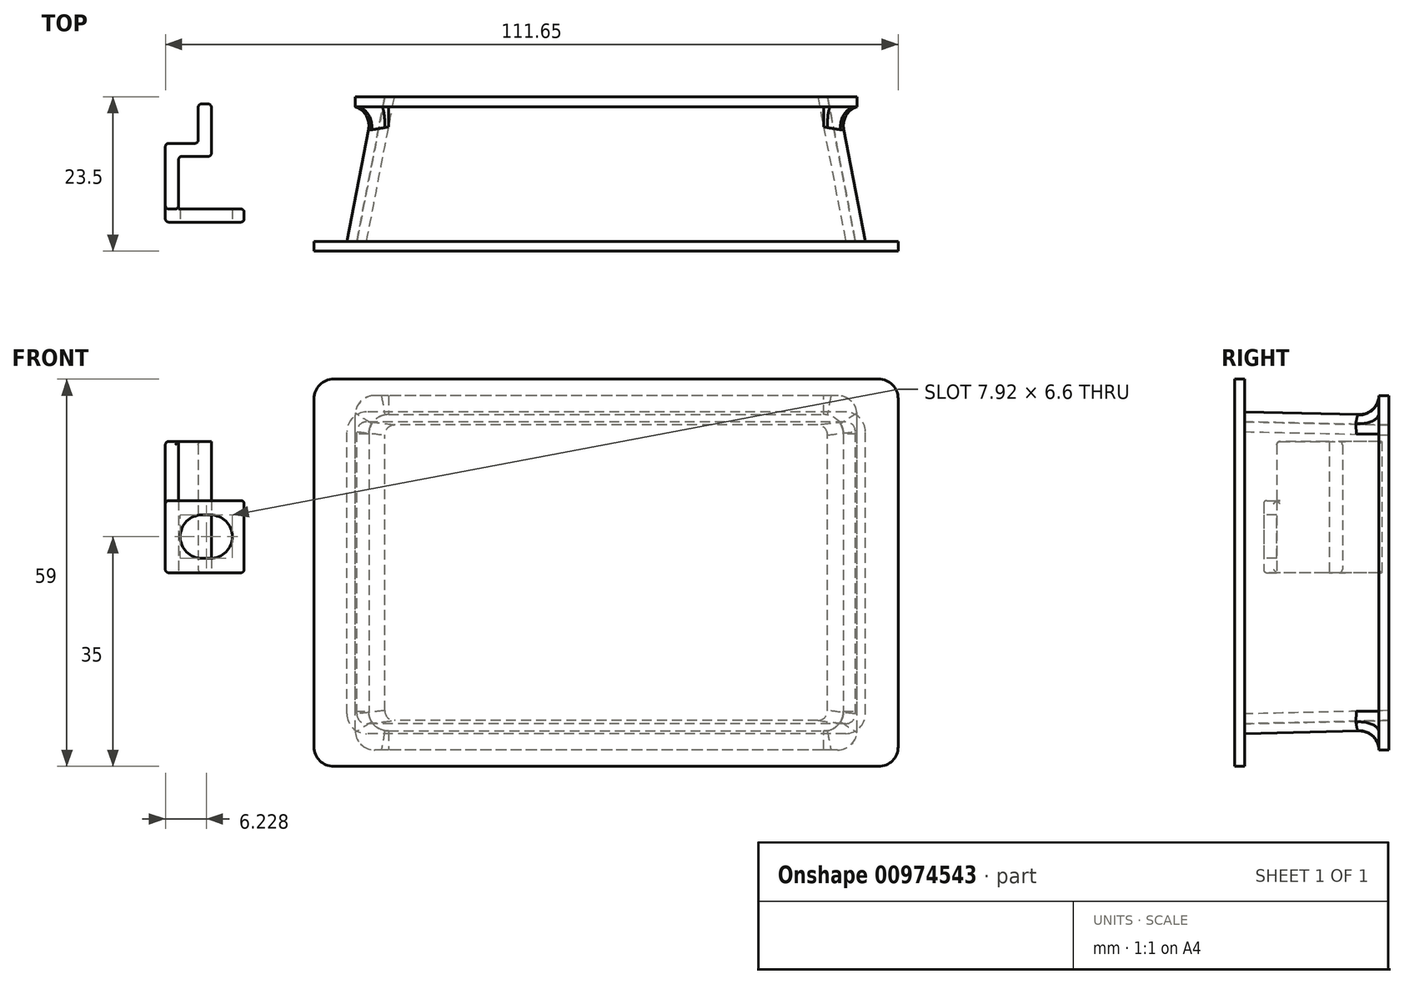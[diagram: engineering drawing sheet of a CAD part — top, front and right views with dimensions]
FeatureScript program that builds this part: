
annotation { "Feature Type Name" : "Feature", "Feature Type Description" : "" }
export const myFeature = defineFeature(function(context is Context, id is Id, definition is map)
    precondition{}
    {
        {
            var Q0;
            Q0=qCreatedBy(makeId("Front.planeOp"),FACE);
            var sketch = newSketch(context, id + "F0", { "sketchPlane" : qUnion([Q0])});
            skLineSegment(sketch, "E0.bottom", {"start": v(32.25, -24) * mm, "end": v(-32.25, -24) * mm});
            skLineSegment(sketch, "E0.top", {"start": v(32.25, 24) * mm, "end": v(-32.25, 24) * mm});
            skLineSegment(sketch, "E0.left", {"start": v(35.25, -21) * mm, "end": v(35.25, 21) * mm});
            skLineSegment(sketch, "E0.right", {"start": v(-35.25, -21) * mm, "end": v(-35.25, 21) * mm});
            skPoint(sketch, "E0.middle", {"position": v(0, 0) * mm});
            skLineSegment(sketch, "E1.0", {"start": v(38.25, 27) * mm, "end": v(-38.25, 27) * mm});
            skLineSegment(sketch, "E1.1", {"start": v(38.25, -27) * mm, "end": v(38.25, 27) * mm});
            skLineSegment(sketch, "E1.2", {"start": v(38.25, -27) * mm, "end": v(-38.25, -27) * mm});
            skLineSegment(sketch, "E1.3", {"start": v(-38.25, -27) * mm, "end": v(-38.25, 27) * mm});
            skPoint(sketch, "E2.visualSharp", {"position": v(35.25, -24) * mm});
            skArc(sketch, "E2.filletArc", {"start": v(32.25, -24) * mm, "mid": v(34.37, -23.12) * mm, "end": v(35.25, -21) * mm});
            skPoint(sketch, "E3.visualSharp", {"position": v(35.25, 24) * mm});
            skArc(sketch, "E3.filletArc", {"start": v(35.25, 21) * mm, "mid": v(34.37, 23.12) * mm, "end": v(32.25, 24) * mm});
            skPoint(sketch, "E4.visualSharp", {"position": v(-35.25, -24) * mm});
            skArc(sketch, "E4.filletArc", {"start": v(-35.25, -21) * mm, "mid": v(-34.37, -23.12) * mm, "end": v(-32.25, -24) * mm});
            skPoint(sketch, "E5.visualSharp", {"position": v(-35.25, 24) * mm});
            skArc(sketch, "E5.filletArc", {"start": v(-32.25, 24) * mm, "mid": v(-34.37, 23.12) * mm, "end": v(-35.25, 21) * mm});
            skSolve(sketch);
        }
        {
            var Q0;
            Q0=qCreatedBy(makeId("Front.planeOp"),FACE);
            cPlane(context, id + "F1", {"entities" : qUnion([Q0]), "cplaneType" : CPlaneType.OFFSET, "offset" : 22 * mm, "width" : 150 * mm, "height" : 150 * mm});
        }
        {
            var Q0;
            Q0=qCreatedBy(id+"F1.planeOp",FACE);
            var sketch = newSketch(context, id + "F2", { "sketchPlane" : qUnion([Q0])});
            skLineSegment(sketch, "E6.bottom", {"start": v(36.5, -24.5) * mm, "end": v(-36.5, -24.5) * mm});
            skLineSegment(sketch, "E6.top", {"start": v(36.5, 24.5) * mm, "end": v(-36.5, 24.5) * mm});
            skLineSegment(sketch, "E6.left", {"start": v(39.5, -21.5) * mm, "end": v(39.5, 21.5) * mm});
            skLineSegment(sketch, "E6.right", {"start": v(-39.5, -21.5) * mm, "end": v(-39.5, 21.5) * mm});
            skPoint(sketch, "E6.middle", {"position": v(0, 0) * mm});
            skLineSegment(sketch, "E7.0", {"start": v(44.5, 29.5) * mm, "end": v(-44.5, 29.5) * mm});
            skLineSegment(sketch, "E7.1", {"start": v(44.5, -29.5) * mm, "end": v(44.5, 29.5) * mm});
            skLineSegment(sketch, "E7.2", {"start": v(44.5, -29.5) * mm, "end": v(-44.5, -29.5) * mm});
            skLineSegment(sketch, "E7.3", {"start": v(-44.5, -29.5) * mm, "end": v(-44.5, 29.5) * mm});
            skPoint(sketch, "E8.visualSharp", {"position": v(39.5, -24.5) * mm});
            skArc(sketch, "E8.filletArc", {"start": v(36.5, -24.5) * mm, "mid": v(38.62, -23.62) * mm, "end": v(39.5, -21.5) * mm});
            skPoint(sketch, "E9.visualSharp", {"position": v(-39.5, -24.5) * mm});
            skArc(sketch, "E9.filletArc", {"start": v(-39.5, -21.5) * mm, "mid": v(-38.62, -23.62) * mm, "end": v(-36.5, -24.5) * mm});
            skPoint(sketch, "E10.visualSharp", {"position": v(-39.5, 24.5) * mm});
            skArc(sketch, "E10.filletArc", {"start": v(-36.5, 24.5) * mm, "mid": v(-38.62, 23.62) * mm, "end": v(-39.5, 21.5) * mm});
            skPoint(sketch, "E11.visualSharp", {"position": v(39.5, 24.5) * mm});
            skArc(sketch, "E11.filletArc", {"start": v(39.5, 21.5) * mm, "mid": v(38.62, 23.62) * mm, "end": v(36.5, 24.5) * mm});
            skSolve(sketch);
        }
        {
            var Q0;
            Q0=makeQuery(id+"F0.imprint","IMPRINT",FACE,{"disambiguationData":[TD([[makeQuery(id+"F0.imprint","IMPRINT",EDGE,{"derivedFrom":sQuery(id+"F0.wireOp",EDGE,"E0.bottom")}),-1.0]])]});
            var Q1;
            Q1=makeQuery(id+"F2.imprint","IMPRINT",FACE,{"disambiguationData":[TD([[makeQuery(id+"F2.imprint","IMPRINT",EDGE,{"derivedFrom":sQuery(id+"F2.wireOp",EDGE,"E6.bottom")}),-1.0]])]});
            var Q2;
            Q2=makeQuery(id+"F0.imprint","IMPRINT",FACE,{"disambiguationData":[TD([[makeQuery(id+"F0.imprint","IMPRINT",EDGE,{"derivedFrom":sQuery(id+"F0.wireOp",EDGE,"E0.bottom")}),-1.0]])]});
            var Q3;
            Q3=makeQuery(id+"F2.imprint","IMPRINT",FACE,{"disambiguationData":[TD([[makeQuery(id+"F2.imprint","IMPRINT",EDGE,{"derivedFrom":sQuery(id+"F2.wireOp",EDGE,"E6.bottom")}),-1.0]])]});
            loft(context, id + "F3", {"sheetProfilesArray" : [{ "sheetProfileEntities" : qUnion([Q0]) }, { "sheetProfileEntities" : qUnion([Q1]) }], "wireProfilesArray" : [{ "wireProfileEntities" : qUnion([Q2]) }, { "wireProfileEntities" : qUnion([Q3]) }]});
        }
        {
            var Q0;
            Q0=makeQuery(id+"F3.opLoft","CAP_FACE",FACE,{"disambiguationData":[OSD([makeQuery(id+"F2.imprint","IMPRINT",FACE,{"disambiguationData":[TD([[makeQuery(id+"F2.imprint","IMPRINT",EDGE,{"derivedFrom":sQuery(id+"F2.wireOp",EDGE,"E6.bottom")}),-1.0]])]})])],"isStart":true});
            var Q1;
            Q1=makeQuery(id+"F3.opLoft","CAP_FACE",FACE,{"disambiguationData":[OSD([makeQuery(id+"F0.imprint","IMPRINT",FACE,{"disambiguationData":[TD([[makeQuery(id+"F0.imprint","IMPRINT",EDGE,{"derivedFrom":sQuery(id+"F0.wireOp",EDGE,"E0.bottom")}),-1.0]])]})])],"isStart":true});
            shell(context, id + "F4", {"entities" : qUnion([Q0, Q1]), "thickness" : 1.5 * mm});
        }
        {
            var Q0;
            Q0=makeQuery(id+"F0.imprint","IMPRINT",FACE,{"disambiguationData":[TD([[makeQuery(id+"F0.imprint","IMPRINT",EDGE,{"derivedFrom":sQuery(id+"F0.wireOp",EDGE,"E0.bottom")}),1.0]])]});
            extrude(context, id + "F5", {"entities" : qUnion([Q0]), "operationType" : NewBodyOperationType.ADD, "depth" : 1.5 * mm, "offsetDistance" : 25 * mm});
        }
        {
            var Q0;
            Q0=makeQuery(id+"F2.imprint","IMPRINT",FACE,{"disambiguationData":[TD([[makeQuery(id+"F2.imprint","IMPRINT",EDGE,{"derivedFrom":sQuery(id+"F2.wireOp",EDGE,"E6.bottom")}),-1.0]])]});
            var sketch = newSketch(context, id + "F6", { "sketchPlane" : qUnion([Q0])});
            skLineSegment(sketch, "E12.0", {"start": v(-37.97, 21.5) * mm, "end": v(-37.97, -21.5) * mm});
            skFitSpline(sketch, "E13.0", {"points": [v(-37.94, -21.48) * mm, v(-37.94, -21.58) * mm, v(-37.92, -21.77) * mm, v(-37.84, -22.06) * mm, v(-37.7, -22.32) * mm, v(-37.53, -22.55) * mm, v(-37.3, -22.74) * mm, v(-37.05, -22.89) * mm, v(-36.78, -22.98) * mm, v(-36.58, -23) * mm, v(-36.48, -23) * mm]});
            skLineSegment(sketch, "E14.0", {"start": v(-36.5, -23) * mm, "end": v(36.5, -23) * mm});
            skLineSegment(sketch, "E15.0", {"start": v(-44.5, -29.5) * mm, "end": v(-44.5, 29.5) * mm});
            skLineSegment(sketch, "E16.0", {"start": v(44.5, -29.5) * mm, "end": v(-44.5, -29.5) * mm});
            skFitSpline(sketch, "E17.0", {"points": [v(36.48, -23) * mm, v(36.58, -23) * mm, v(36.77, -22.98) * mm, v(37.15, -22.86) * mm, v(37.55, -22.57) * mm, v(37.87, -22.07) * mm, v(37.94, -21.68) * mm, v(37.94, -21.48) * mm]});
            skLineSegment(sketch, "E18.0", {"start": v(37.97, -21.5) * mm, "end": v(37.97, 21.5) * mm});
            skLineSegment(sketch, "E19.0", {"start": v(44.5, -29.5) * mm, "end": v(44.5, 29.5) * mm});
            skFitSpline(sketch, "E20.0", {"points": [v(37.94, 21.48) * mm, v(37.94, 21.58) * mm, v(37.92, 21.77) * mm, v(37.84, 22.06) * mm, v(37.7, 22.32) * mm, v(37.53, 22.55) * mm, v(37.3, 22.74) * mm, v(37.05, 22.89) * mm, v(36.78, 22.98) * mm, v(36.58, 23) * mm, v(36.48, 23) * mm]});
            skLineSegment(sketch, "E21.0", {"start": v(44.5, 29.5) * mm, "end": v(-44.5, 29.5) * mm});
            skLineSegment(sketch, "E22.0", {"start": v(36.5, 23) * mm, "end": v(-36.5, 23) * mm});
            skFitSpline(sketch, "E23.0", {"points": [v(-36.48, 23) * mm, v(-36.58, 23) * mm, v(-36.77, 22.98) * mm, v(-37.15, 22.86) * mm, v(-37.55, 22.57) * mm, v(-37.87, 22.07) * mm, v(-37.94, 21.68) * mm, v(-37.94, 21.48) * mm]});
            skSolve(sketch);
        }
        {
            var Q0;
            Q0 = qSketchRegion(id + "F6", true);
            extrude(context, id + "F7", {"entities" : qUnion([Q0]), "operationType" : NewBodyOperationType.ADD, "depth" : 1.5 * mm, "offsetDistance" : 25 * mm});
        }
        {
            var Q0;
            Q0=makeQuery(id+"F5.opExtrude","SWEPT_EDGE",EDGE,{"disambiguationData":[OSD([sQuery(id+"F0.wireOp",EDGE,"E1.0"),sQuery(id+"F0.wireOp",EDGE,"E1.1")])]});
            var Q1;
            Q1=makeQuery(id+"F5.opExtrude","SWEPT_EDGE",EDGE,{"disambiguationData":[OSD([sQuery(id+"F0.wireOp",EDGE,"E1.0"),sQuery(id+"F0.wireOp",EDGE,"E1.3")])]});
            var Q2;
            Q2=makeQuery(id+"F5.opExtrude","SWEPT_EDGE",EDGE,{"disambiguationData":[OSD([sQuery(id+"F0.wireOp",EDGE,"E1.2"),sQuery(id+"F0.wireOp",EDGE,"E1.3")])]});
            var Q3;
            Q3=makeQuery(id+"F5.opExtrude","SWEPT_EDGE",EDGE,{"disambiguationData":[OSD([sQuery(id+"F0.wireOp",EDGE,"E1.1"),sQuery(id+"F0.wireOp",EDGE,"E1.2")])]});
            var Q4;
            Q4=makeQuery(id+"F7.opExtrude","SWEPT_EDGE",EDGE,{"disambiguationData":[OSD([sQuery(id+"FlOIacHDovV2RVo_1.wireOp",EDGE,"569a9f4c-9bc3-4d06-a376-a9eeb0658dbe.1"),sQuery(id+"FlOIacHDovV2RVo_1.wireOp",EDGE,"569a9f4c-9bc3-4d06-a376-a9eeb0658dbe.2")])]});
            var Q5;
            Q5=makeQuery(id+"F7.opExtrude","SWEPT_EDGE",EDGE,{"disambiguationData":[OSD([sQuery(id+"FlOIacHDovV2RVo_1.wireOp",EDGE,"569a9f4c-9bc3-4d06-a376-a9eeb0658dbe.1"),sQuery(id+"FlOIacHDovV2RVo_1.wireOp",EDGE,"569a9f4c-9bc3-4d06-a376-a9eeb0658dbe.4")])]});
            var Q6;
            Q6=makeQuery(id+"F7.opExtrude","SWEPT_EDGE",EDGE,{"disambiguationData":[OSD([sQuery(id+"FlOIacHDovV2RVo_1.wireOp",EDGE,"569a9f4c-9bc3-4d06-a376-a9eeb0658dbe.3"),sQuery(id+"FlOIacHDovV2RVo_1.wireOp",EDGE,"569a9f4c-9bc3-4d06-a376-a9eeb0658dbe.4")])]});
            var Q7;
            Q7=makeQuery(id+"F7.opExtrude","SWEPT_EDGE",EDGE,{"disambiguationData":[OSD([sQuery(id+"FlOIacHDovV2RVo_1.wireOp",EDGE,"569a9f4c-9bc3-4d06-a376-a9eeb0658dbe.2"),sQuery(id+"FlOIacHDovV2RVo_1.wireOp",EDGE,"569a9f4c-9bc3-4d06-a376-a9eeb0658dbe.3")])]});
            var Q8;
            Q8=makeQuery(id+"F7.opExtrude","SWEPT_EDGE",EDGE,{"disambiguationData":[OSD([sQuery(id+"F6.wireOp",EDGE,"E19.0"),sQuery(id+"F6.wireOp",EDGE,"E21.0")])]});
            var Q9;
            Q9=makeQuery(id+"F7.opExtrude","SWEPT_EDGE",EDGE,{"disambiguationData":[OSD([sQuery(id+"F6.wireOp",EDGE,"E16.0"),sQuery(id+"F6.wireOp",EDGE,"E19.0")])]});
            var Q10;
            Q10=makeQuery(id+"F7.opExtrude","SWEPT_EDGE",EDGE,{"disambiguationData":[OSD([sQuery(id+"F6.wireOp",EDGE,"E15.0"),sQuery(id+"F6.wireOp",EDGE,"E16.0")])]});
            var Q11;
            Q11=makeQuery(id+"F7.opExtrude","SWEPT_EDGE",EDGE,{"disambiguationData":[OSD([sQuery(id+"F6.wireOp",EDGE,"E15.0"),sQuery(id+"F6.wireOp",EDGE,"E21.0")])]});
            fillet(context, id + "F8", {"entities" : qUnion([Q0, Q1, Q2, Q3, Q4, Q5, Q6, Q7, Q8, Q9, Q10, Q11]), "radius" : 3 * mm, "tangentPropagation" : true, "allowEdgeOverflow" : false});
        }
        {
            var Q0;
            {var subQ0=sQuery(id+"F0.wireOp",EDGE,"E5.filletArc");var subQ1=sQuery(id+"F0.wireOp",EDGE,"E4.filletArc");var subQ2=sQuery(id+"F0.wireOp",EDGE,"E3.filletArc");var subQ3=sQuery(id+"F0.wireOp",EDGE,"E2.filletArc");var subQ4=sQuery(id+"F0.wireOp",EDGE,"E0.right");var subQ5=sQuery(id+"F0.wireOp",EDGE,"E0.left");var subQ6=sQuery(id+"F0.wireOp",EDGE,"E0.top");var subQ7=sQuery(id+"F0.wireOp",EDGE,"E0.bottom");Q0=makeQuery(id+"F5.boolean.opBoolean","INTERSECT",EDGE,{"derivedFrom":[makeQuery(id+"F3.opLoft","SWEPT_FACE",FACE,{"disambiguationData":[OSD([subQ7,subQ6,subQ5,subQ4,subQ3,subQ2,subQ1,subQ0,sQuery(id+"F2.wireOp",EDGE,"E6.bottom"),sQuery(id+"F2.wireOp",EDGE,"E6.top"),sQuery(id+"F2.wireOp",EDGE,"E6.left"),sQuery(id+"F2.wireOp",EDGE,"E6.right"),sQuery(id+"F2.wireOp",EDGE,"E8.filletArc"),sQuery(id+"F2.wireOp",EDGE,"E9.filletArc"),sQuery(id+"F2.wireOp",EDGE,"E10.filletArc"),sQuery(id+"F2.wireOp",EDGE,"E11.filletArc")])]}),makeQuery(id+"F5.opExtrude","CAP_FACE",FACE,{"disambiguationData":[OSD([subQ7,subQ6,subQ5,subQ4,sQuery(id+"F0.wireOp",EDGE,"E1.0"),sQuery(id+"F0.wireOp",EDGE,"E1.1"),sQuery(id+"F0.wireOp",EDGE,"E1.2"),sQuery(id+"F0.wireOp",EDGE,"E1.3"),subQ3,subQ2,subQ1,subQ0])],"isStart":false})]});}
            fillet(context, id + "F9", {"entities" : qUnion([Q0]), "radius" : 3 * mm, "tangentPropagation" : true, "allowEdgeOverflow" : false});
        }
        {
            var Q0;
            Q0=qCreatedBy(makeId("Top.planeOp"),FACE);
            var sketch = newSketch(context, id + "F10", { "sketchPlane" : qUnion([Q0])});
            skLineSegment(sketch, "E24", {"start": v(-55.15, -17.08) * mm, "end": v(-65.15, -17.08) * mm});
            skLineSegment(sketch, "E25", {"start": v(-67.15, -17.08) * mm, "end": v(-67.15, -19.08) * mm});
            skLineSegment(sketch, "E26", {"start": v(-67.15, -19.08) * mm, "end": v(-55.15, -19.08) * mm});
            skLineSegment(sketch, "E27", {"start": v(-55.15, -19.08) * mm, "end": v(-55.15, -17.08) * mm});
            skLineSegment(sketch, "E28", {"start": v(-67.15, -17.08) * mm, "end": v(-67.15, -7.08) * mm});
            skLineSegment(sketch, "E29", {"start": v(-65.15, -9.08) * mm, "end": v(-65.15, -17.08) * mm});
            skLineSegment(sketch, "E30", {"start": v(-67.15, -7.08) * mm, "end": v(-62.15, -7.08) * mm});
            skLineSegment(sketch, "E31", {"start": v(-60.15, -7.08) * mm, "end": v(-60.15, -9.08) * mm});
            skLineSegment(sketch, "E32", {"start": v(-60.15, -9.08) * mm, "end": v(-65.15, -9.08) * mm});
            skLineSegment(sketch, "E33", {"start": v(-60.15, -7.08) * mm, "end": v(-60.15, -1.08) * mm});
            skLineSegment(sketch, "E34", {"start": v(-60.15, -1.08) * mm, "end": v(-62.15, -1.08) * mm});
            skLineSegment(sketch, "E35", {"start": v(-62.15, -1.08) * mm, "end": v(-62.15, -7.08) * mm});
            skLineSegment(sketch, "E36", {"start": v(-65.15, -17.08) * mm, "end": v(-67.15, -17.08) * mm});
            skSolve(sketch);
        }
        {
            var Q0;
            {var subQ0=sQuery(id+"F10.wireOp",EDGE,"E25");Q0=makeQuery(id+"F10.imprint","IMPRINT",FACE,{"disambiguationData":[TD([[makeQuery(id+"F10.imprint","IMPRINT",EDGE,{"derivedFrom":subQ0}),1.0]])]});}
            extrude(context, id + "F11", {"entities" : qUnion([Q0]), "depth" : 11 * mm, "offsetDistance" : 25 * mm});
        }
        {
            var Q0;
            Q0=makeQuery(id+"F11.opExtrude","SWEPT_FACE",FACE,{"disambiguationData":[OSD([sQuery(id+"F10.wireOp",EDGE,"E26")])]});
            var sketch = newSketch(context, id + "F12", { "sketchPlane" : qUnion([Q0])});
            skPoint(sketch, "E37.endSnap0", {"position": v(-55.15, 5.5) * mm});
            skLineSegment(sketch, "E38", {"start": v(-53.25, 5.5) * mm, "end": v(-69.92, 5.5) * mm, "construction": true});
            skArc(sketch, "E39", {"start": v(-60.26, 2.2) * mm, "mid": v(-56.96, 5.5) * mm, "end": v(-60.26, 8.8) * mm});
            skArc(sketch, "E40", {"start": v(-61.58, 8.8) * mm, "mid": v(-64.88, 5.5) * mm, "end": v(-61.58, 2.2) * mm});
            skLineSegment(sketch, "E41", {"start": v(-60.26, 2.2) * mm, "end": v(-61.58, 2.2) * mm});
            skLineSegment(sketch, "E42", {"start": v(-60.26, 8.8) * mm, "end": v(-61.58, 8.8) * mm});
            skSolve(sketch);
        }
        {
            var Q0;
            Q0=makeQuery(id+"F12.imprint","IMPRINT",FACE,{"disambiguationData":[TD([[makeQuery(id+"F12.imprint","IMPRINT",EDGE,{"derivedFrom":sQuery(id+"F12.wireOp",EDGE,"E39")}),1.0]])]});
            extrude(context, id + "F13", {"entities" : qUnion([Q0]), "operationType" : NewBodyOperationType.REMOVE, "endBound" : BoundingType.THROUGH_ALL, "oppositeDirection" : true, "depth" : 25 * mm, "offsetDistance" : 25 * mm});
        }
        {
            var Q0;
            Q0=makeQuery(id+"F10.imprint","IMPRINT",FACE,{"disambiguationData":[TD([[makeQuery(id+"F10.imprint","IMPRINT",EDGE,{"derivedFrom":sQuery(id+"F10.wireOp",EDGE,"E28")}),-1.0]])]});
            extrude(context, id + "F14", {"entities" : qUnion([Q0]), "operationType" : NewBodyOperationType.ADD, "depth" : 20 * mm, "offsetDistance" : 25 * mm});
        }
        {
            var Q0;
            Q0=makeQuery(id+"F11.opExtrude","CAP_EDGE",EDGE,{"disambiguationData":[OSD([sQuery(id+"F10.wireOp",EDGE,"E26")])],"isStart":false});
            var Q1;
            Q1=makeQuery(id+"F11.opExtrude","SWEPT_EDGE",EDGE,{"disambiguationData":[OSD([sQuery(id+"F10.wireOp",EDGE,"E26"),sQuery(id+"F10.wireOp",EDGE,"E27")])]});
            var Q2;
            Q2=makeQuery(id+"F11.opExtrude","CAP_EDGE",EDGE,{"disambiguationData":[OSD([sQuery(id+"F10.wireOp",EDGE,"E26")])],"isStart":true});
            var Q3;
            Q3=makeQuery(id+"F11.opExtrude","SWEPT_EDGE",EDGE,{"disambiguationData":[OSD([sQuery(id+"F10.wireOp",EDGE,"E25"),sQuery(id+"F10.wireOp",EDGE,"E26")])]});
            var Q4;
            Q4=makeQuery(id+"F14.boolean.opBoolean","MERGE",EDGE,{"derivedFrom":[makeQuery(id+"F11.opExtrude","CAP_EDGE",EDGE,{"disambiguationData":[OSD([sQuery(id+"F10.wireOp",EDGE,"E25")])],"isStart":true}),makeQuery(id+"F14.opExtrude","CAP_EDGE",EDGE,{"disambiguationData":[OSD([sQuery(id+"F10.wireOp",EDGE,"E28")])],"isStart":true})]});
            var Q5;
            Q5=makeQuery(id+"F14.opExtrude","CAP_EDGE",EDGE,{"disambiguationData":[OSD([sQuery(id+"F10.wireOp",EDGE,"E30")])],"isStart":true});
            var Q6;
            Q6=makeQuery(id+"F14.opExtrude","CAP_EDGE",EDGE,{"disambiguationData":[OSD([sQuery(id+"F10.wireOp",EDGE,"E35")])],"isStart":true});
            var Q7;
            Q7=makeQuery(id+"F14.opExtrude","SWEPT_EDGE",EDGE,{"disambiguationData":[OSD([sQuery(id+"F10.wireOp",EDGE,"E34"),sQuery(id+"F10.wireOp",EDGE,"E35")])]});
            var Q8;
            Q8=makeQuery(id+"F14.opExtrude","CAP_EDGE",EDGE,{"disambiguationData":[OSD([sQuery(id+"F10.wireOp",EDGE,"E35")])],"isStart":false});
            var Q9;
            Q9=makeQuery(id+"F14.opExtrude","CAP_EDGE",EDGE,{"disambiguationData":[OSD([sQuery(id+"F10.wireOp",EDGE,"E30")])],"isStart":false});
            var Q10;
            Q10=makeQuery(id+"F14.opExtrude","CAP_EDGE",EDGE,{"disambiguationData":[OSD([sQuery(id+"F10.wireOp",EDGE,"E28")])],"isStart":false});
            var Q11;
            Q11=makeQuery(id+"F14.opExtrude","SWEPT_EDGE",EDGE,{"disambiguationData":[OSD([sQuery(id+"F10.wireOp",EDGE,"E28"),sQuery(id+"F10.wireOp",EDGE,"E30")])]});
            var Q12;
            Q12=makeQuery(id+"F14.opExtrude","SWEPT_EDGE",EDGE,{"disambiguationData":[OSD([sQuery(id+"F10.wireOp",EDGE,"E30"),sQuery(id+"F10.wireOp",EDGE,"E35")])]});
            var Q13;
            Q13=makeQuery(id+"F14.opExtrude","SWEPT_EDGE",EDGE,{"disambiguationData":[OSD([sQuery(id+"F10.wireOp",EDGE,"E25"),sQuery(id+"F10.wireOp",EDGE,"E28"),sQuery(id+"F10.wireOp",EDGE,"E36")])]});
            var Q14;
            Q14=makeQuery(id+"F11.opExtrude","CAP_EDGE",EDGE,{"disambiguationData":[OSD([sQuery(id+"F10.wireOp",EDGE,"E25")])],"isStart":false});
            var Q15;
            Q15=makeQuery(id+"F14.opExtrude","CAP_EDGE",EDGE,{"disambiguationData":[OSD([sQuery(id+"F10.wireOp",EDGE,"E36")])],"isStart":false});
            var Q16;
            Q16=makeQuery(id+"F11.opExtrude","CAP_EDGE",EDGE,{"disambiguationData":[OSD([sQuery(id+"F10.wireOp",EDGE,"E27")])],"isStart":false});
            var Q17;
            Q17=makeQuery(id+"F11.opExtrude","CAP_EDGE",EDGE,{"disambiguationData":[OSD([sQuery(id+"F10.wireOp",EDGE,"E27")])],"isStart":true});
            var Q18;
            Q18=makeQuery(id+"F14.opExtrude","SWEPT_EDGE",EDGE,{"disambiguationData":[OSD([sQuery(id+"F10.wireOp",EDGE,"E31"),sQuery(id+"F10.wireOp",EDGE,"E32")])]});
            var Q19;
            Q19=makeQuery(id+"F14.opExtrude","SWEPT_EDGE",EDGE,{"disambiguationData":[OSD([sQuery(id+"F10.wireOp",EDGE,"E29"),sQuery(id+"F10.wireOp",EDGE,"E32")])]});
            var Q20;
            {var subQ0=sQuery(id+"F10.wireOp",EDGE,"E36");var subQ1=sQuery(id+"F10.wireOp",EDGE,"E24");var subQ2=sQuery(id+"F10.wireOp",EDGE,"E29");Q20=makeQuery(id+"F14.boolean.opBoolean","SPLIT",EDGE,{"disambiguationData":[topologyDisambiguationEdgeConnected([makeQuery(id+"F11.opExtrude","SWEPT_FACE",FACE,{"disambiguationData":[OSD([subQ1,subQ0])]})])],"derivedFrom":makeQuery(id+"F14.opExtrude","SWEPT_EDGE",EDGE,{"disambiguationData":[OSD([subQ1,subQ2,subQ0])]})});}
            var Q21;
            Q21=makeQuery(id+"F14.opExtrude","SWEPT_EDGE",EDGE,{"disambiguationData":[OSD([sQuery(id+"F10.wireOp",EDGE,"E33"),sQuery(id+"F10.wireOp",EDGE,"E34")])]});
            var Q22;
            Q22=makeQuery(id+"F11.opExtrude","SWEPT_EDGE",EDGE,{"disambiguationData":[OSD([sQuery(id+"F10.wireOp",EDGE,"E24"),sQuery(id+"F10.wireOp",EDGE,"E27")])]});
            fillet(context, id + "F15", {"entities" : qUnion([Q0, Q1, Q2, Q3, Q4, Q5, Q6, Q7, Q8, Q9, Q10, Q11, Q12, Q13, Q14, Q15, Q16, Q17, Q18, Q19, Q20, Q21, Q22]), "radius" : 0.5 * mm, "tangentPropagation" : true, "allowEdgeOverflow" : false});
        }
    });
